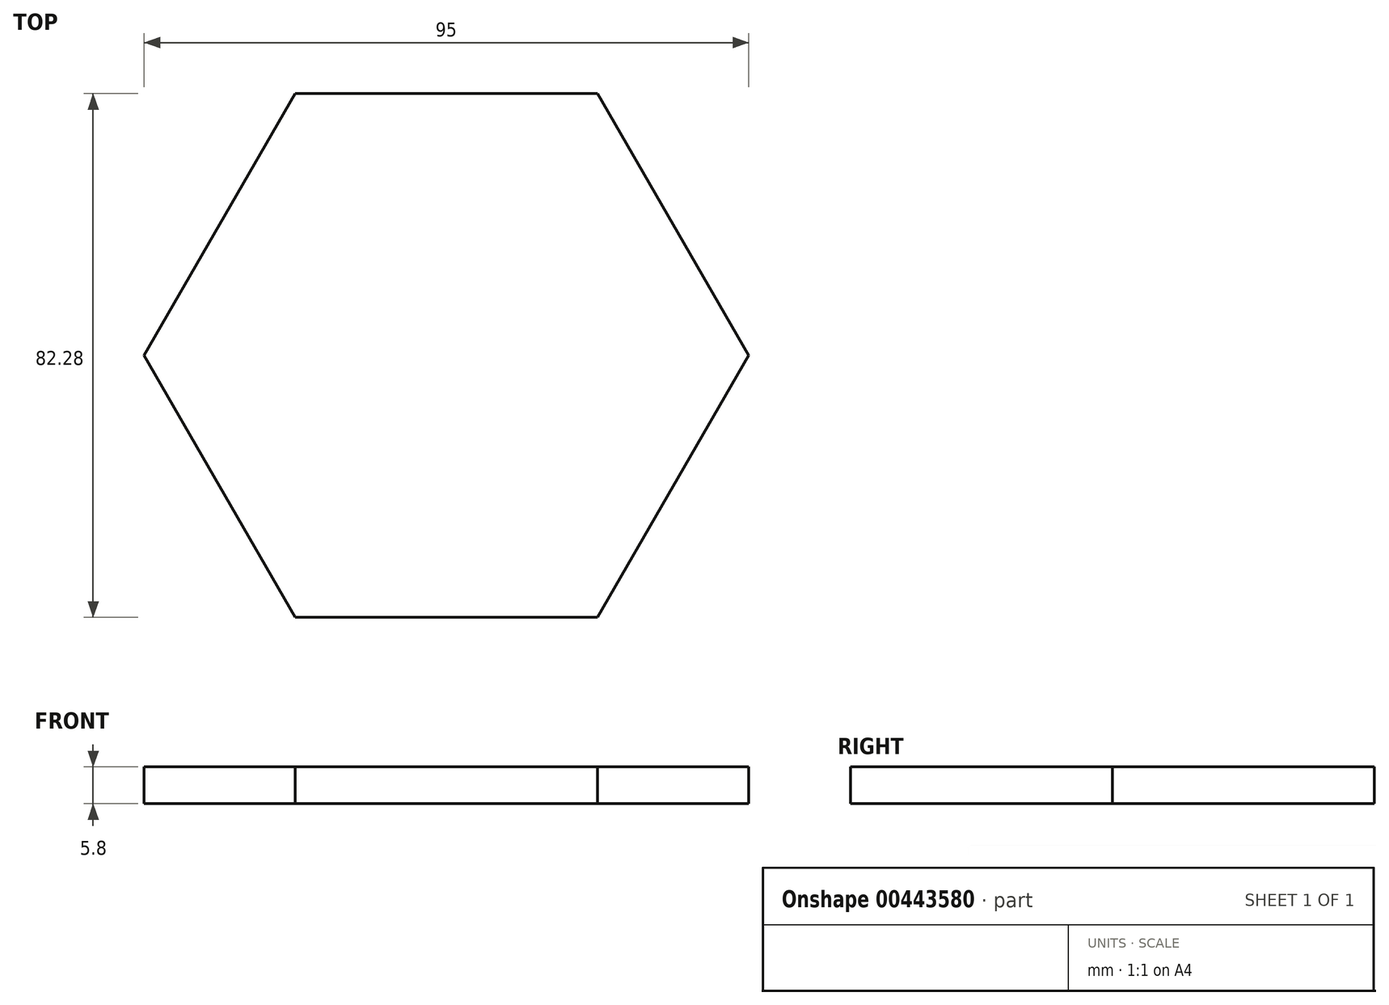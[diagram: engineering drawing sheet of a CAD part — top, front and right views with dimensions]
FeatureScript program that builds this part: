
annotation { "Feature Type Name" : "Feature", "Feature Type Description" : "" }
export const myFeature = defineFeature(function(context is Context, id is Id, definition is map)
    precondition{}
    {
        {
            var Q0;
            Q0=qCreatedBy(makeId("Top.planeOp"),FACE);
            var sketch = newSketch(context, id + "F0", { "sketchPlane" : qUnion([Q0])});
            skLineSegment(sketch, "E0", {"start": v(-23.75, 41.14) * mm, "end": v(-47.5, 0) * mm});
            skLineSegment(sketch, "E1", {"start": v(23.75, 41.14) * mm, "end": v(47.5, 0) * mm});
            skLineSegment(sketch, "E2", {"start": v(-47.5, 0) * mm, "end": v(-23.75, -41.14) * mm});
            skLineSegment(sketch, "E3", {"start": v(47.5, 0) * mm, "end": v(23.75, -41.14) * mm});
            skLineSegment(sketch, "E4", {"start": v(23.75, -41.14) * mm, "end": v(-23.75, -41.14) * mm});
            skCircle(sketch, "E5", {"center": v(0, 0) * mm, "radius": 41.14 * mm, "construction": true});
            skLineSegment(sketch, "E6", {"start": v(-23.75, 41.14) * mm, "end": v(23.75, 41.14) * mm});
            skLineSegment(sketch, "E7.top", {"start": v(-23.75, 121.14) * mm, "end": v(23.75, 121.14) * mm});
            skLineSegment(sketch, "E7.left", {"start": v(23.75, 41.14) * mm, "end": v(23.75, 121.14) * mm});
            skLineSegment(sketch, "E7.right", {"start": v(-23.75, 41.14) * mm, "end": v(-23.75, 121.14) * mm});
            skLineSegment(sketch, "E8.bottom", {"start": v(-23.75, 41.14) * mm, "end": v(-23.75, 41.14) * mm});
            skSolve(sketch);
        }
        {
            var Q0;
            Q0=makeQuery(id+"F0.imprint","IMPRINT",FACE,{"disambiguationData":[TD([[makeQuery(id+"F0.imprint","IMPRINT",EDGE,{"derivedFrom":sQuery(id+"F0.wireOp",EDGE,"E0")}),1.0]])]});
            var Q1;
            Q1=makeQuery(id+"F0.imprint","IMPRINT",FACE,{"disambiguationData":[TD([[makeQuery(id+"F0.imprint","IMPRINT",EDGE,{"derivedFrom":sQuery(id+"F0.wireOp",EDGE,"E6")}),1.0]])]});
            extrude(context, id + "F1", {"entities" : qUnion([Q0, Q1]), "depth" : 5.8 * mm});
        }
    });
